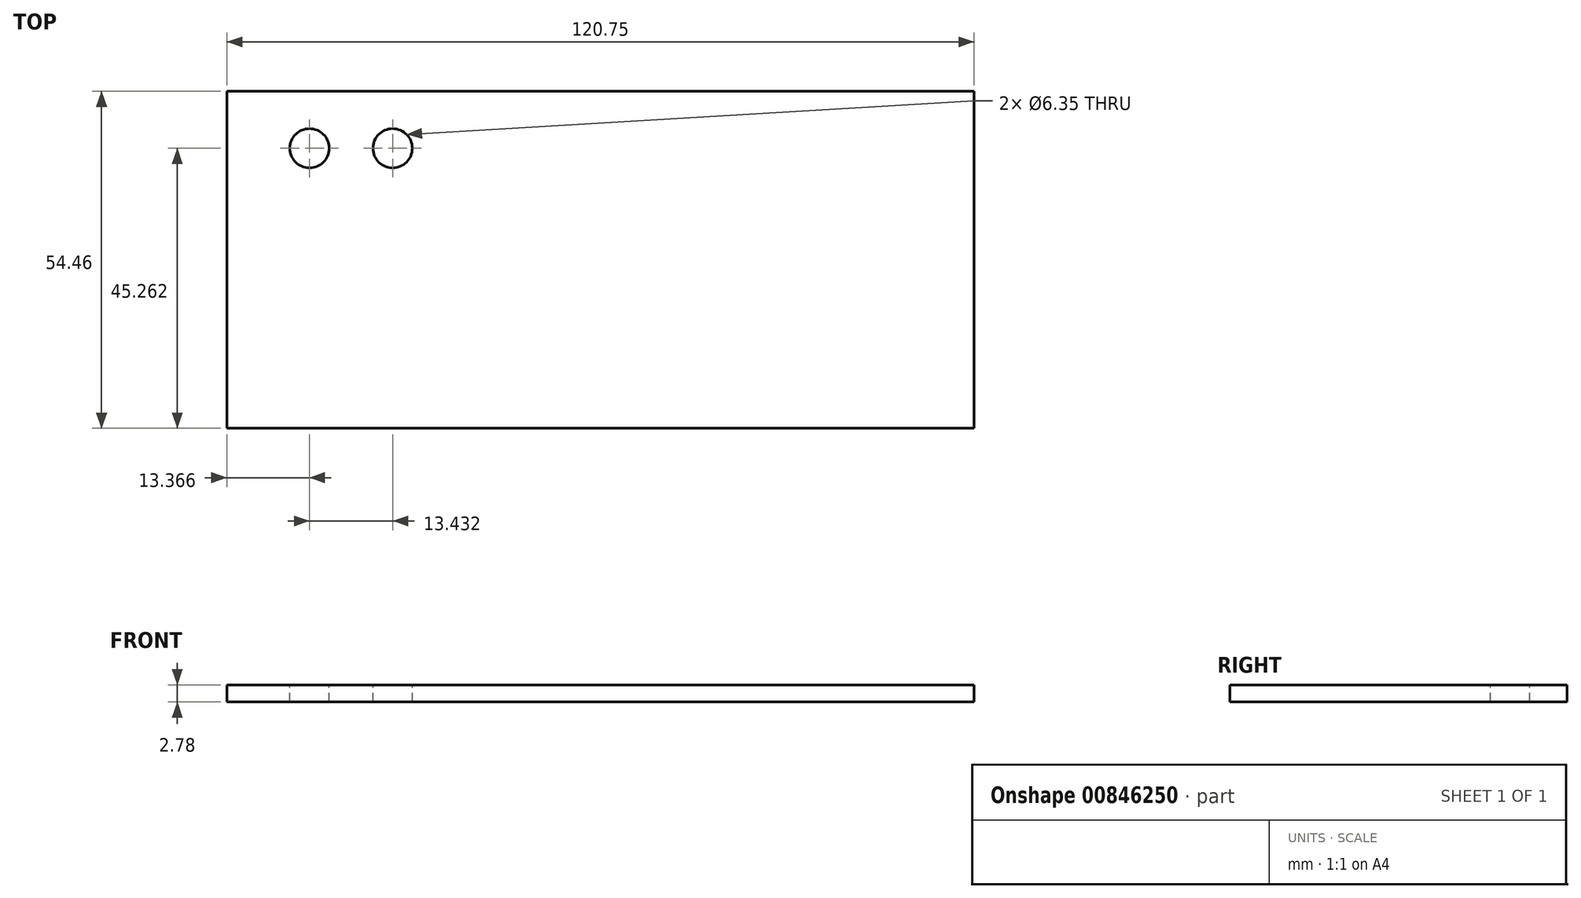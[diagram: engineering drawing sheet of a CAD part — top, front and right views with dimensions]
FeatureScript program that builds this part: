
annotation { "Feature Type Name" : "Feature", "Feature Type Description" : "" }
export const myFeature = defineFeature(function(context is Context, id is Id, definition is map)
    precondition{}
    {
        {
            var Q0;
            Q0=qCreatedBy(makeId("Top.planeOp"),FACE);
            var sketch = newSketch(context, id + "F0", { "sketchPlane" : qUnion([Q0])});
            skLineSegment(sketch, "E0", {"start": v(0, 0) * mm, "end": v(120.75, 0) * mm});
            skLineSegment(sketch, "E1", {"start": v(120.75, 0) * mm, "end": v(120.75, -54.46) * mm});
            skLineSegment(sketch, "E2", {"start": v(120.75, -54.46) * mm, "end": v(0, -54.46) * mm});
            skLineSegment(sketch, "E3", {"start": v(0, -54.46) * mm, "end": v(0, 0) * mm});
            skSolve(sketch);
        }
        {
            var Q0;
            Q0=makeQuery(id+"F0.imprint","IMPRINT",FACE,{"disambiguationData":[TD([[makeQuery(id+"F0.imprint","IMPRINT",EDGE,{"derivedFrom":sQuery(id+"F0.wireOp",EDGE,"E0")}),-1.0]])]});
            extrude(context, id + "F1", {"entities" : qUnion([Q0]), "depth" : 2.78 * mm, "offsetDistance" : 25.4 * mm});
        }
        {
            var Q0;
            Q0=makeQuery(id+"F1.opExtrude","CAP_FACE",FACE,{"disambiguationData":[OSD([sQuery(id+"F0.wireOp",EDGE,"E0"),sQuery(id+"F0.wireOp",EDGE,"E1"),sQuery(id+"F0.wireOp",EDGE,"E2"),sQuery(id+"F0.wireOp",EDGE,"E3")])],"isStart":false});
            var sketch = newSketch(context, id + "F2", { "sketchPlane" : qUnion([Q0])});
            skLineSegment(sketch, "E4", {"start": v(0, 0) * mm, "end": v(0, -9.2) * mm});
            skLineSegment(sketch, "E5", {"start": v(0, -9.2) * mm, "end": v(120.75, -9.2) * mm});
            skLineSegment(sketch, "E6", {"start": v(120.75, -9.2) * mm, "end": v(120.75, -18.25) * mm});
            skLineSegment(sketch, "E7", {"start": v(120.75, -18.25) * mm, "end": v(0, -18.25) * mm});
            skLineSegment(sketch, "E8", {"start": v(0, -18.25) * mm, "end": v(0, -27.23) * mm});
            skLineSegment(sketch, "E9", {"start": v(0, -27.23) * mm, "end": v(120.75, -27.23) * mm});
            skLineSegment(sketch, "E10", {"start": v(120.75, -27.23) * mm, "end": v(120.75, -36.35) * mm});
            skLineSegment(sketch, "E11", {"start": v(120.75, -36.35) * mm, "end": v(0, -36.35) * mm});
            skLineSegment(sketch, "E12", {"start": v(0, -36.35) * mm, "end": v(0, -45.4) * mm});
            skLineSegment(sketch, "E13", {"start": v(0, -45.4) * mm, "end": v(120.75, -45.4) * mm});
            skLineSegment(sketch, "E14", {"start": v(120.75, -45.4) * mm, "end": v(120.75, -54.46) * mm});
            skLineSegment(sketch, "E15", {"start": v(120.75, -54.46) * mm, "end": v(107.4, -54.46) * mm});
            skLineSegment(sketch, "E16", {"start": v(107.4, -54.46) * mm, "end": v(93.96, -54.46) * mm});
            skLineSegment(sketch, "E17", {"start": v(93.96, -54.46) * mm, "end": v(80.53, -54.46) * mm});
            skLineSegment(sketch, "E18", {"start": v(80.53, -54.46) * mm, "end": v(67.1, -54.46) * mm});
            skLineSegment(sketch, "E19", {"start": v(67.1, -54.46) * mm, "end": v(53.66, -54.46) * mm});
            skLineSegment(sketch, "E20", {"start": v(53.66, -54.46) * mm, "end": v(40.23, -54.46) * mm});
            skLineSegment(sketch, "E21", {"start": v(40.23, -54.46) * mm, "end": v(26.8, -54.46) * mm});
            skLineSegment(sketch, "E22", {"start": v(26.8, -54.46) * mm, "end": v(13.37, -54.46) * mm});
            skLineSegment(sketch, "E23", {"start": v(13.37, -54.46) * mm, "end": v(0, -54.46) * mm});
            skLineSegment(sketch, "E24", {"start": v(13.37, -54.46) * mm, "end": v(13.37, 0) * mm});
            skLineSegment(sketch, "E25", {"start": v(13.37, 0) * mm, "end": v(26.8, 0) * mm});
            skLineSegment(sketch, "E26", {"start": v(26.8, 0) * mm, "end": v(26.8, -54.46) * mm});
            skLineSegment(sketch, "E27", {"start": v(40.23, -54.46) * mm, "end": v(40.23, 0) * mm});
            skLineSegment(sketch, "E28", {"start": v(53.66, -54.46) * mm, "end": v(53.66, 0) * mm});
            skLineSegment(sketch, "E29", {"start": v(53.66, 0) * mm, "end": v(67.1, 0) * mm});
            skLineSegment(sketch, "E30", {"start": v(67.1, 0) * mm, "end": v(67.1, -54.46) * mm});
            skLineSegment(sketch, "E31", {"start": v(80.53, -54.46) * mm, "end": v(80.53, 0) * mm});
            skLineSegment(sketch, "E32", {"start": v(80.53, 0) * mm, "end": v(93.96, 0) * mm});
            skLineSegment(sketch, "E33", {"start": v(93.96, 0) * mm, "end": v(93.96, -54.46) * mm});
            skLineSegment(sketch, "E34", {"start": v(107.4, -54.46) * mm, "end": v(107.4, 0) * mm});
            skCircle(sketch, "E35", {"center": v(13.37, -9.2) * mm, "radius": 2.7 * mm});
            skCircle(sketch, "E36", {"center": v(26.8, -9.2) * mm, "radius": 2.7 * mm});
            skSolve(sketch);
        }
        {
            var Q0;
            Q0=sQuery(id+"F2.wireOp",VERTEX,"E35.center");
            var Q1;
            Q1=sQuery(id+"F2.wireOp",VERTEX,"E36.center");
            var Q2;
            Q2=makeQuery(id+"F1.opExtrude","SWEPT_BODY",BODY,{"disambiguationData":[OSD([sQuery(id+"F0.wireOp",EDGE,"E0"),sQuery(id+"F0.wireOp",EDGE,"E1"),sQuery(id+"F0.wireOp",EDGE,"E2"),sQuery(id+"F0.wireOp",EDGE,"E3")])]});
            hole(context, id + "F3", {"style" : HoleStyle.SIMPLE, "endStyle" : HoleEndStyle.THROUGH, "holeDiameter" : 6.35 * mm, "majorDiameter" : 6.35 * mm, "isTappedThrough" : true, "tappedDepth" : 12.7 * mm, "tapClearance" : 3, "locations" : qUnion([Q0, Q1]), "scope" : qUnion([Q2])});
        }
    });
